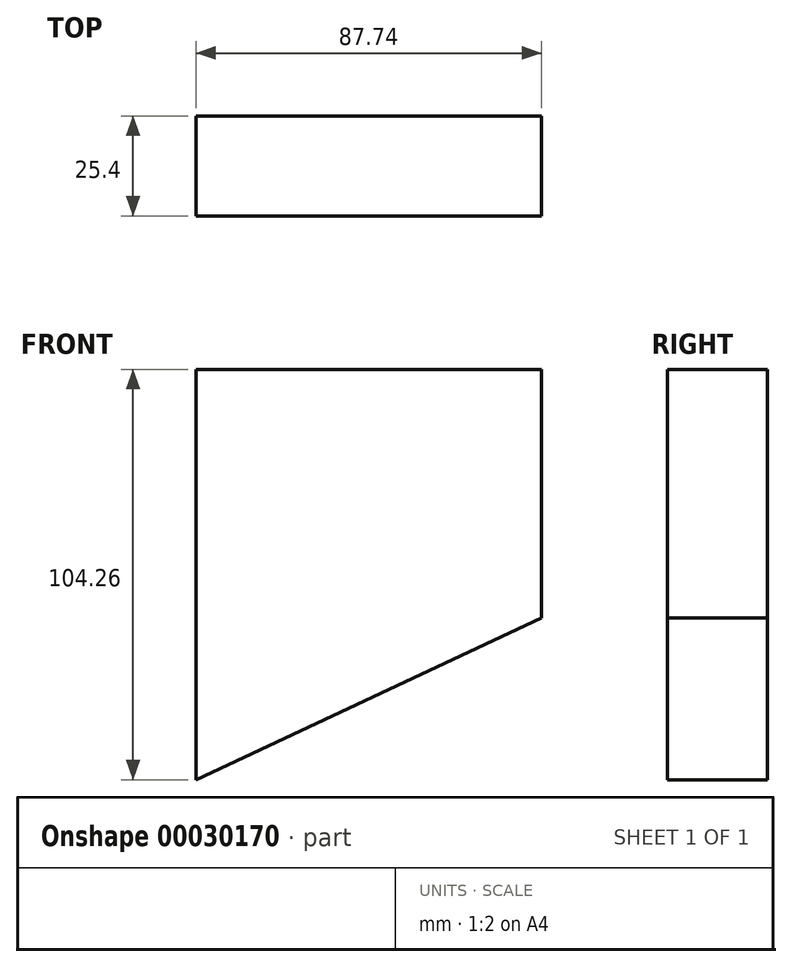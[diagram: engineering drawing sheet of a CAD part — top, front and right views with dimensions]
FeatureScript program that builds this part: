
annotation { "Feature Type Name" : "Feature", "Feature Type Description" : "" }
export const myFeature = defineFeature(function(context is Context, id is Id, definition is map)
    precondition{}
    {
        {
            var Q0;
            Q0=qCreatedBy(makeId("Front.planeOp"),FACE);
            var sketch = newSketch(context, id + "F0", { "sketchPlane" : qUnion([Q0])});
            skLineSegment(sketch, "E0", {"start": v(-49.23, -59.58) * mm, "end": v(-49.23, 44.68) * mm});
            skLineSegment(sketch, "E1", {"start": v(-49.23, 44.68) * mm, "end": v(38.51, 44.68) * mm});
            skLineSegment(sketch, "E2", {"start": v(38.51, 44.68) * mm, "end": v(38.51, -18.45) * mm});
            skLineSegment(sketch, "E3", {"start": v(38.51, -18.45) * mm, "end": v(-49.23, -59.58) * mm});
            skSolve(sketch);
        }
        {
            var Q0;
            Q0=makeQuery(id+"F0.imprint","IMPRINT",FACE,{"disambiguationData":[TD([[makeQuery(id+"F0.imprint","IMPRINT",EDGE,{"derivedFrom":sQuery(id+"F0.wireOp",EDGE,"E0")}),-1.0]])]});
            extrude(context, id + "F1", {"entities" : qUnion([Q0]), "depth" : 25.4 * mm});
        }
    });
